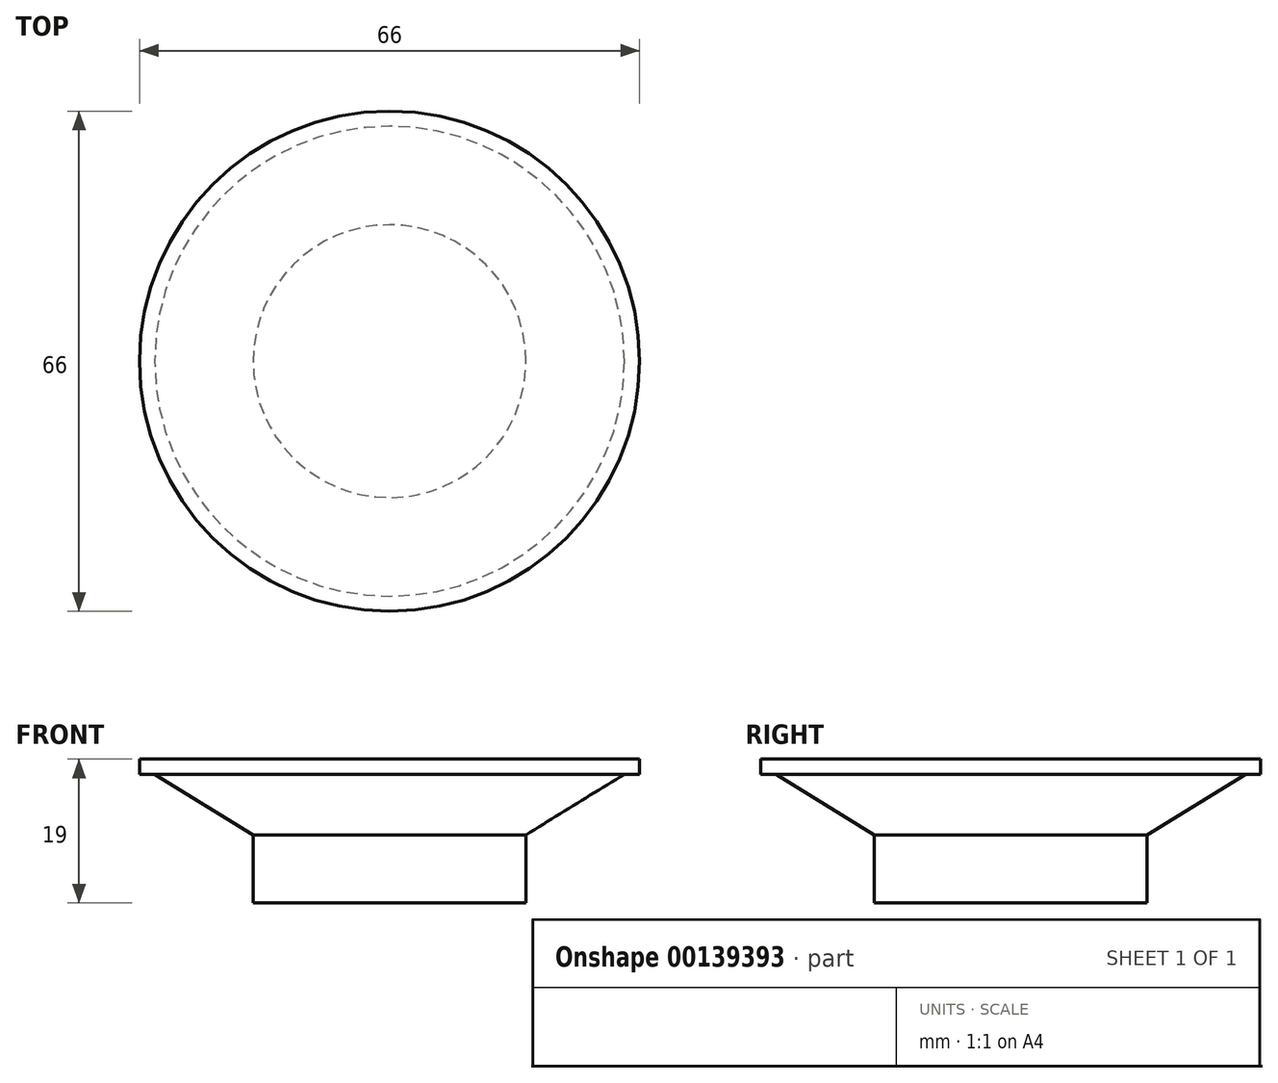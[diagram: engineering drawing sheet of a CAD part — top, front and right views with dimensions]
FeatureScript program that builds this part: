
annotation { "Feature Type Name" : "Feature", "Feature Type Description" : "" }
export const myFeature = defineFeature(function(context is Context, id is Id, definition is map)
    precondition{}
    {
        {
            var Q0;
            Q0=qCreatedBy(makeId("Front.planeOp"),FACE);
            var sketch = newSketch(context, id + "F0", { "sketchPlane" : qUnion([Q0])});
            skLineSegment(sketch, "E0", {"start": v(0, 0) * mm, "end": v(18, 0) * mm});
            skLineSegment(sketch, "E1", {"start": v(18, 0) * mm, "end": v(18, 9) * mm});
            skLineSegment(sketch, "E2", {"start": v(0, 19) * mm, "end": v(0, 0) * mm});
            skPoint(sketch, "E3.start.orphan", {"position": v(31, 29.57) * mm});
            skLineSegment(sketch, "E4", {"start": v(0, 19) * mm, "end": v(33, 19) * mm});
            skLineSegment(sketch, "E5", {"start": v(33, 19) * mm, "end": v(33, 17) * mm});
            skLineSegment(sketch, "E6", {"start": v(33, 17) * mm, "end": v(31, 17) * mm});
            skLineSegment(sketch, "E7", {"start": v(18, 9) * mm, "end": v(31, 17) * mm});
            skSolve(sketch);
        }
        {
            var Q0;
            Q0 = qSketchRegion(id + "F0", true);
            var Q1;
            Q1=sQuery(id+"F0.wireOp",EDGE,"E2");
            revolve(context, id + "F1", {"entities" : qUnion([Q0]), "axis" : qUnion([Q1]), "revolveType" : RevolveType.FULL});
        }
    });
